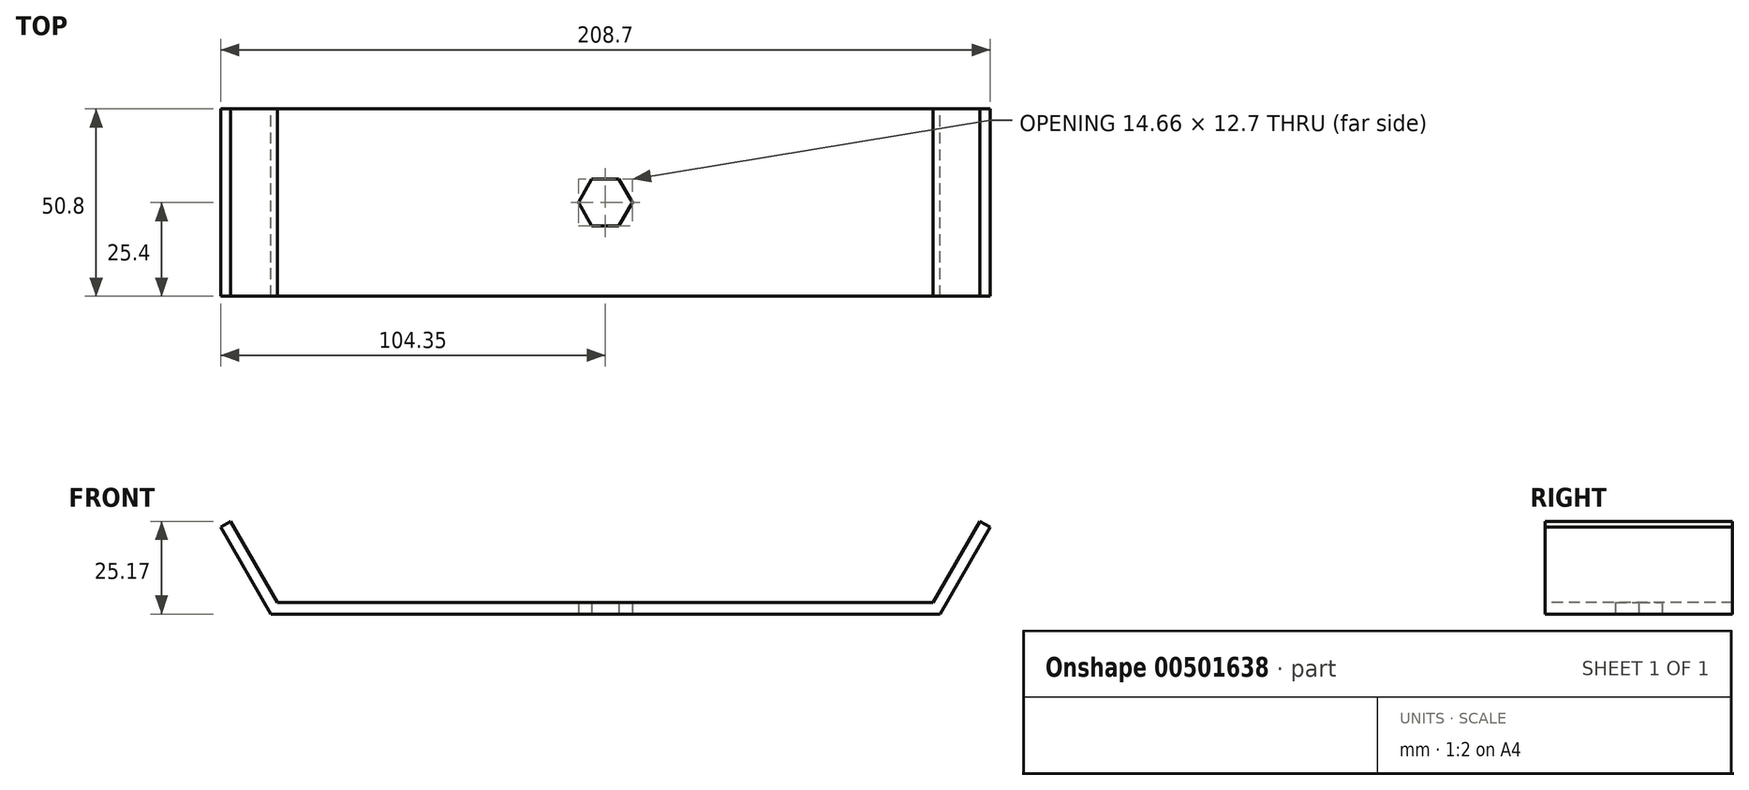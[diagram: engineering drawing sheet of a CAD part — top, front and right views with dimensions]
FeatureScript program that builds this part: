
annotation { "Feature Type Name" : "Feature", "Feature Type Description" : "" }
export const myFeature = defineFeature(function(context is Context, id is Id, definition is map)
    precondition{}
    {
        {
            var Q0;
            Q0=qCreatedBy(makeId("Top.planeOp"),FACE);
            var sketch = newSketch(context, id + "F0", { "sketchPlane" : qUnion([Q0])});
            skLineSegment(sketch, "E0.bottom", {"start": v(-88.9, 25.4) * mm, "end": v(88.9, 25.4) * mm});
            skLineSegment(sketch, "E0.top", {"start": v(-88.9, -25.4) * mm, "end": v(88.9, -25.4) * mm});
            skLineSegment(sketch, "E0.left", {"start": v(-88.9, 25.4) * mm, "end": v(-88.9, -25.4) * mm});
            skLineSegment(sketch, "E0.right", {"start": v(88.9, 25.4) * mm, "end": v(88.9, -25.4) * mm});
            skPoint(sketch, "E0.middle", {"position": v(0, 0) * mm});
            skCircle(sketch, "E1.cCircle", {"center": v(0, 0) * mm, "radius": 6.35 * mm, "construction": true});
            skLineSegment(sketch, "E1.0", {"start": v(-7.33, 0) * mm, "end": v(-3.67, 6.35) * mm});
            skLineSegment(sketch, "E1.1", {"start": v(-3.67, 6.35) * mm, "end": v(3.67, 6.35) * mm});
            skLineSegment(sketch, "E1.2", {"start": v(3.67, 6.35) * mm, "end": v(7.33, 0) * mm});
            skLineSegment(sketch, "E1.3", {"start": v(7.33, 0) * mm, "end": v(3.67, -6.35) * mm});
            skLineSegment(sketch, "E1.4", {"start": v(3.67, -6.35) * mm, "end": v(-3.67, -6.35) * mm});
            skLineSegment(sketch, "E1.5", {"start": v(-3.67, -6.35) * mm, "end": v(-7.33, 0) * mm});
            skPoint(sketch, "E1.0.midPoint", {"position": v(-5.5, 3.18) * mm});
            skSolve(sketch);
        }
        {
            var Q0;
            Q0=qSketchRegion(id+"F0",true);
            extrude(context, id + "F1", {"entities" : qUnion([Q0]), "depth" : 3.17 * mm});
        }
        {
            var Q0;
            Q0=qCreatedBy(makeId("Front.planeOp"),FACE);
            var sketch = newSketch(context, id + "F2", { "sketchPlane" : qUnion([Q0])});
            skLineSegment(sketch, "E2", {"start": v(-90.73, 0) * mm, "end": v(-104.35, 23.58) * mm});
            skLineSegment(sketch, "E3", {"start": v(-88.9, 3.18) * mm, "end": v(-101.6, 25.17) * mm});
            skLineSegment(sketch, "E4", {"start": v(-101.6, 25.17) * mm, "end": v(-104.35, 23.58) * mm});
            skLineSegment(sketch, "E5.MirrorCS", {"start": v(101.6, 25.17) * mm, "end": v(104.35, 23.58) * mm});
            skLineSegment(sketch, "E6.MirrorCS", {"start": v(90.73, 0) * mm, "end": v(104.35, 23.58) * mm});
            skLineSegment(sketch, "E7.MirrorCS", {"start": v(88.9, 3.17) * mm, "end": v(101.6, 25.17) * mm});
            skLineSegment(sketch, "E8", {"start": v(-90.73, 0) * mm, "end": v(-88.9, 0) * mm});
            skLineSegment(sketch, "E9", {"start": v(-88.9, 0) * mm, "end": v(-88.9, 3.18) * mm});
            skLineSegment(sketch, "E10.MirrorCS", {"start": v(88.9, 0) * mm, "end": v(88.9, 3.18) * mm});
            skLineSegment(sketch, "E11.MirrorCS", {"start": v(90.73, 0) * mm, "end": v(88.9, 0) * mm});
            skSolve(sketch);
        }
        {
            var Q0;
            Q0=qSketchRegion(id+"F2",true);
            extrude(context, id + "F3", {"entities" : qUnion([Q0]), "operationType" : NewBodyOperationType.ADD, "endBound" : BoundingType.SYMMETRIC, "depth" : 50.8 * mm});
        }
    });
